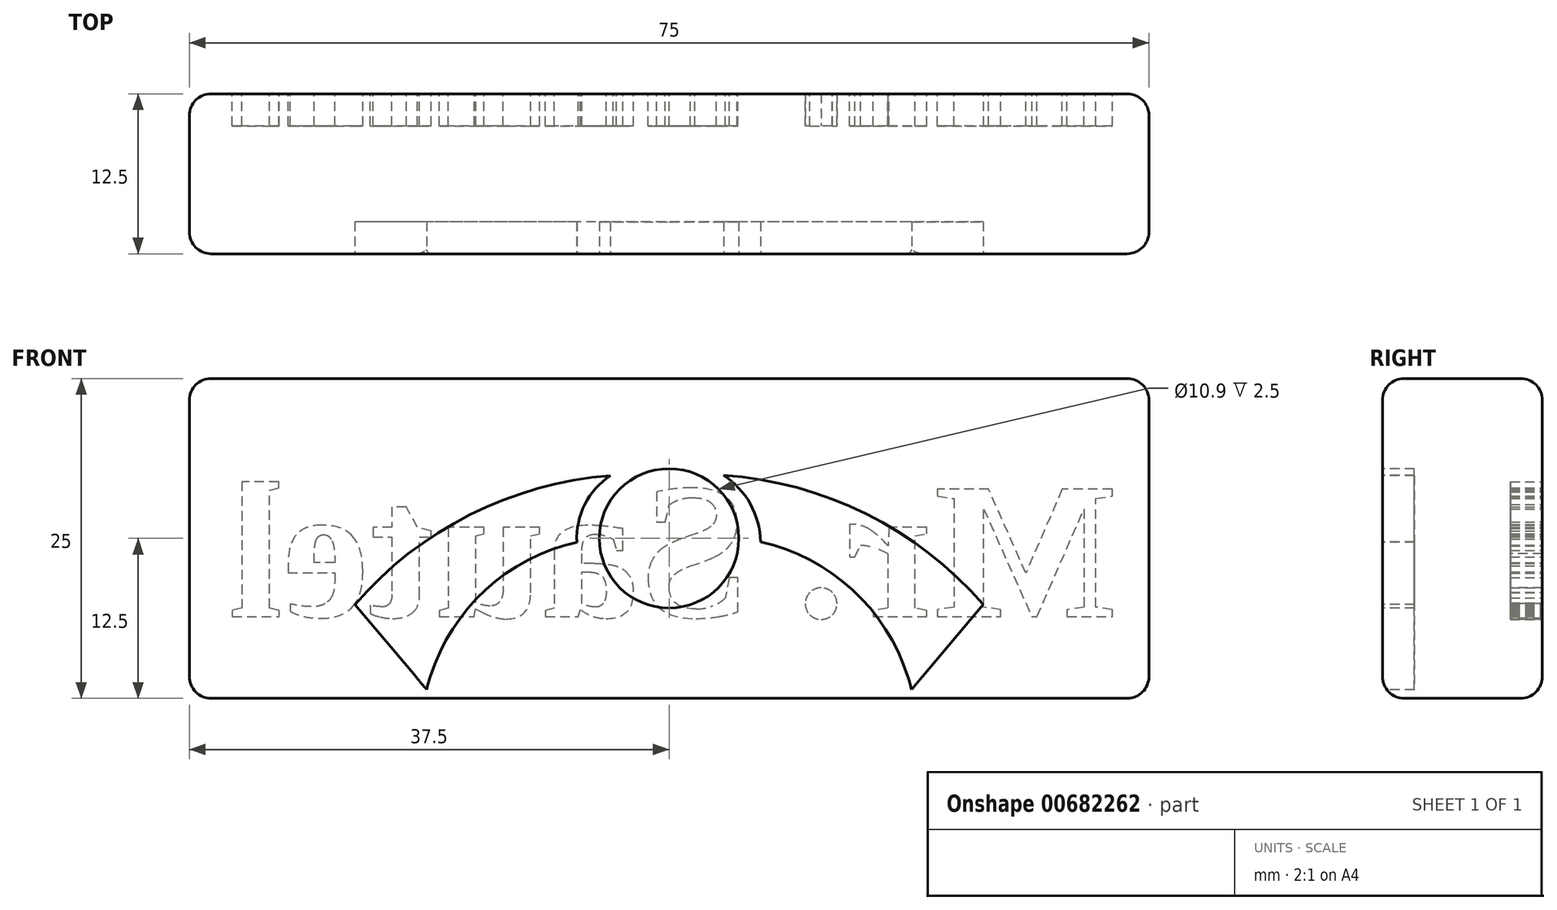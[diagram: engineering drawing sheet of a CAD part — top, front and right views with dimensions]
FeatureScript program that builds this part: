
annotation { "Feature Type Name" : "Feature", "Feature Type Description" : "" }
export const myFeature = defineFeature(function(context is Context, id is Id, definition is map)
    precondition{}
    {
        {
            var Q0;
            Q0=qCreatedBy(makeId("Top.planeOp"),FACE);
            var sketch = newSketch(context, id + "F0", { "sketchPlane" : qUnion([Q0])});
            skLineSegment(sketch, "E0.bottom", {"start": v(0, 0) * mm, "end": v(150, 0) * mm});
            skLineSegment(sketch, "E0.top", {"start": v(0, -25) * mm, "end": v(150, -25) * mm});
            skLineSegment(sketch, "E0.left", {"start": v(0, 0) * mm, "end": v(0, -25) * mm});
            skLineSegment(sketch, "E0.right", {"start": v(150, 0) * mm, "end": v(150, -25) * mm});
            skSolve(sketch);
        }
        {
            var Q0;
            Q0=makeQuery(id+"F0.imprint","IMPRINT",FACE,{"disambiguationData":[TD([[makeQuery(id+"F0.imprint","IMPRINT",EDGE,{"derivedFrom":sQuery(id+"F0.wireOp",EDGE,"E0.bottom")}),-1.0]])]});
            extrude(context, id + "F1", {"entities" : qUnion([Q0]), "depth" : 50 * mm, "offsetDistance" : 25 * mm});
        }
        {
            var Q0;
            Q0=makeQuery(id+"F1.opExtrude","CAP_EDGE",EDGE,{"disambiguationData":[OSD([sQuery(id+"F0.wireOp",EDGE,"E0.top")])],"isStart":false});
            var Q1;
            Q1=makeQuery(id+"F1.opExtrude","CAP_EDGE",EDGE,{"disambiguationData":[OSD([sQuery(id+"F0.wireOp",EDGE,"E0.bottom")])],"isStart":false});
            var Q2;
            Q2=makeQuery(id+"F1.opExtrude","CAP_EDGE",EDGE,{"disambiguationData":[OSD([sQuery(id+"F0.wireOp",EDGE,"E0.right")])],"isStart":false});
            var Q3;
            Q3=makeQuery(id+"F1.opExtrude","CAP_EDGE",EDGE,{"disambiguationData":[OSD([sQuery(id+"F0.wireOp",EDGE,"E0.left")])],"isStart":false});
            var Q4;
            Q4=makeQuery(id+"F1.opExtrude","SWEPT_EDGE",EDGE,{"disambiguationData":[OSD([sQuery(id+"F0.wireOp",EDGE,"E0.top"),sQuery(id+"F0.wireOp",EDGE,"E0.left")])]});
            var Q5;
            Q5=makeQuery(id+"F1.opExtrude","SWEPT_EDGE",EDGE,{"disambiguationData":[OSD([sQuery(id+"F0.wireOp",EDGE,"E0.bottom"),sQuery(id+"F0.wireOp",EDGE,"E0.left")])]});
            var Q6;
            Q6=makeQuery(id+"F1.opExtrude","CAP_EDGE",EDGE,{"disambiguationData":[OSD([sQuery(id+"F0.wireOp",EDGE,"E0.left")])],"isStart":true});
            var Q7;
            Q7=makeQuery(id+"F1.opExtrude","SWEPT_EDGE",EDGE,{"disambiguationData":[OSD([sQuery(id+"F0.wireOp",EDGE,"E0.top"),sQuery(id+"F0.wireOp",EDGE,"E0.right")])]});
            var Q8;
            Q8=makeQuery(id+"F1.opExtrude","SWEPT_EDGE",EDGE,{"disambiguationData":[OSD([sQuery(id+"F0.wireOp",EDGE,"E0.bottom"),sQuery(id+"F0.wireOp",EDGE,"E0.right")])]});
            var Q9;
            Q9=makeQuery(id+"F1.opExtrude","CAP_EDGE",EDGE,{"disambiguationData":[OSD([sQuery(id+"F0.wireOp",EDGE,"E0.right")])],"isStart":true});
            var Q10;
            Q10=makeQuery(id+"F1.opExtrude","CAP_EDGE",EDGE,{"disambiguationData":[OSD([sQuery(id+"F0.wireOp",EDGE,"E0.bottom")])],"isStart":true});
            var Q11;
            Q11=makeQuery(id+"F1.opExtrude","CAP_EDGE",EDGE,{"disambiguationData":[OSD([sQuery(id+"F0.wireOp",EDGE,"E0.top")])],"isStart":true});
            fillet(context, id + "F2", {"entities" : qUnion([Q0, Q1, Q2, Q3, Q4, Q5, Q6, Q7, Q8, Q9, Q10, Q11]), "radius" : 3.4 * mm, "tangentPropagation" : true, "allowEdgeOverflow" : false});
        }
        {
            var Q0;
            Q0=makeQuery(id+"F1.opExtrude","SWEPT_FACE",FACE,{"disambiguationData":[OSD([sQuery(id+"F0.wireOp",EDGE,"E0.bottom")])]});
            var sketch = newSketch(context, id + "F3", { "sketchPlane" : qUnion([Q0])});
            skText(sketch, "E1", { "text": "Mr. Sautel", "fontName": "Tinos-Bold.ttf"});
            const initialGuessF3  = {"E1": [-0.1448, 0.01276, 1, 0, 0.02191]};
            skSetInitialGuess(sketch, initialGuessF3);
            skSolve(sketch);
        }
        {
            var Q0;
            Q0 = qSketchRegion(id + "F3", true);
            extrude(context, id + "F4", {"entities" : qUnion([Q0]), "operationType" : NewBodyOperationType.REMOVE, "oppositeDirection" : true, "depth" : 5 * mm, "offsetDistance" : 25 * mm});
        }
        {
            var Q0;
            Q0=makeQuery(id+"F1.opExtrude","SWEPT_FACE",FACE,{"disambiguationData":[OSD([sQuery(id+"F0.wireOp",EDGE,"E0.top")])]});
            var sketch = newSketch(context, id + "F5", { "sketchPlane" : qUnion([Q0])});
            skCircle(sketch, "E2", {"center": v(75, 25) * mm, "radius": 10.9 * mm});
            skPoint(sketch, "E2.centerSnap0", {"position": v(3.4, 25) * mm});
            skPoint(sketch, "E2.centerSnap1", {"position": v(75, 46.6) * mm});
            skArc(sketch, "E3", {"start": v(64.1, 25) * mm, "mid": v(46.87, 17.44) * mm, "end": v(37.1, 1.36) * mm});
            skPoint(sketch, "E4.startSnap0", {"position": v(160.9, 28.75) * mm});
            skArc(sketch, "E5", {"start": v(112.9, 1.36) * mm, "mid": v(103.13, 17.44) * mm, "end": v(85.9, 25) * mm});
            skLineSegment(sketch, "E6", {"start": v(37.1, 1.36) * mm, "end": v(25.87, 14.64) * mm});
            skLineSegment(sketch, "E7", {"start": v(112.9, 1.36) * mm, "end": v(124.1, 14.64) * mm});
            skArc(sketch, "E8", {"start": v(70.62, 34.98) * mm, "mid": v(46.01, 29.71) * mm, "end": v(25.87, 14.64) * mm});
            skArc(sketch, "E9", {"start": v(124.1, 14.64) * mm, "mid": v(103.97, 29.7) * mm, "end": v(79.38, 34.98) * mm});
            skArc(sketch, "E10", {"start": v(65.84, 34.8) * mm, "mid": v(61.84, 30.3) * mm, "end": v(60.58, 24.41) * mm});
            skArc(sketch, "E11", {"start": v(89.3, 24.44) * mm, "mid": v(87.7, 30.37) * mm, "end": v(83.52, 34.85) * mm});
            skSolve(sketch);
        }
        {
            var Q0;
            {var subQ0=sQuery(id+"F5.wireOp",EDGE,"E2");var subQ1=makeQuery(id+"F5.imprint","INTERSECT",VERTEX,{"derivedFrom":[subQ0,sQuery(id+"F5.wireOp",EDGE,"E5")]});Q0=makeQuery(id+"F5.imprint","IMPRINT",FACE,{"disambiguationData":[TD([[makeQuery(id+"F5.imprint","IMPRINT",EDGE,{"disambiguationData":[TD([[subQ1,-1.0]])],"derivedFrom":subQ0}),1.0]])]});}
            var Q1;
            {var subQ0=sQuery(id+"F5.wireOp",EDGE,"E3");Q1=makeQuery(id+"F5.imprint","IMPRINT",FACE,{"disambiguationData":[TD([[makeQuery(id+"F5.imprint","IMPRINT",EDGE,{"derivedFrom":subQ0}),-1.0]])]});}
            var Q2;
            {var subQ0=sQuery(id+"F5.wireOp",EDGE,"E5");Q2=makeQuery(id+"F5.imprint","IMPRINT",FACE,{"disambiguationData":[TD([[makeQuery(id+"F5.imprint","IMPRINT",EDGE,{"derivedFrom":subQ0}),-1.0]])]});}
            var Q3;
            {var subQ0=sQuery(id+"F5.wireOp",EDGE,"E10");Q3=makeQuery(id+"F5.imprint","IMPRINT",FACE,{"disambiguationData":[TD([[makeQuery(id+"F5.imprint","IMPRINT",EDGE,{"derivedFrom":subQ0}),-1.0]])]});}
            var Q4;
            {var subQ0=sQuery(id+"F5.wireOp",EDGE,"E9");var subQ10=makeQuery(id+"F5.imprint","IMPRINT",VERTEX,{"derivedFrom":subQ0});Q4=makeQuery(id+"F5.imprint","IMPRINT",FACE,{"disambiguationData":[TD([[makeQuery(id+"F5.imprint","IMPRINT",EDGE,{"disambiguationData":[TD([[subQ10,1.0]])],"derivedFrom":subQ0}),1.0]])]});}
            var Q5;
            {var subQ0=sQuery(id+"F5.wireOp",EDGE,"E11");Q5=makeQuery(id+"F5.imprint","IMPRINT",FACE,{"disambiguationData":[TD([[makeQuery(id+"F5.imprint","IMPRINT",EDGE,{"derivedFrom":subQ0}),-1.0]])]});}
            extrude(context, id + "F6", {"entities" : qUnion([Q0, Q1, Q2, Q3, Q4, Q5]), "operationType" : NewBodyOperationType.REMOVE, "oppositeDirection" : true, "depth" : 5 * mm, "offsetDistance" : 25 * mm});
        }
        {
            var Q0;
            Q0=makeQuery(id+"F1.opExtrude","SWEPT_BODY",BODY,{"disambiguationData":[OSD([sQuery(id+"F0.wireOp",EDGE,"E0.bottom"),sQuery(id+"F0.wireOp",EDGE,"E0.top"),sQuery(id+"F0.wireOp",EDGE,"E0.left"),sQuery(id+"F0.wireOp",EDGE,"E0.right")])]});
            var Q1;
            Q1=qCreatedBy(makeId("Origin.pointOp"),VERTEX);
            transform(context, id + "F7", {"entities" : qUnion([Q0]), "transformType" : TransformType.SCALE_UNIFORMLY, "scale" : 0.5, "scalePoint" : qUnion([Q1]), "makeCopy" : false});
        }
    });
